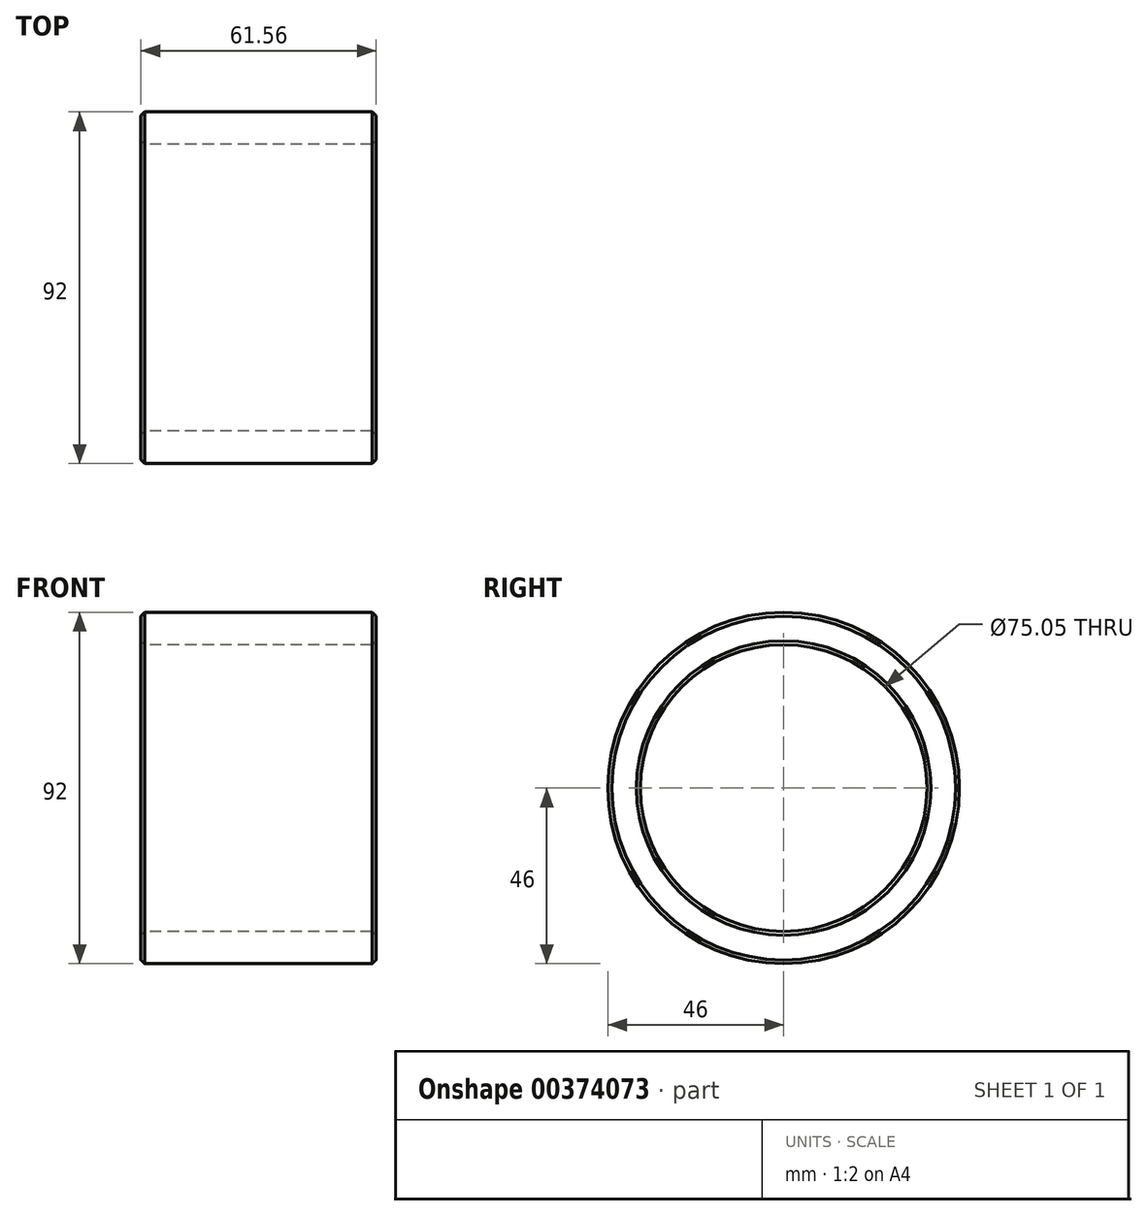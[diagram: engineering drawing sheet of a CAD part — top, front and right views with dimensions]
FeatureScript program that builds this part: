
annotation { "Feature Type Name" : "Feature", "Feature Type Description" : "" }
export const myFeature = defineFeature(function(context is Context, id is Id, definition is map)
    precondition{}
    {
        {
            var Q0;
            Q0=qCreatedBy(makeId("Right.planeOp"),FACE);
            var sketch = newSketch(context, id + "F0", { "sketchPlane" : qUnion([Q0])});
            skCircle(sketch, "E0", {"center": v(0, 0) * mm, "radius": 37.53 * mm});
            skCircle(sketch, "E1", {"center": v(0, 0) * mm, "radius": 46 * mm});
            skSolve(sketch);
        }
        {
            var Q0;
            Q0=qSketchRegion(id+"F0",true);
            extrude(context, id + "F1", {"entities" : qUnion([Q0]), "offsetDistance" : 25 * mm, "depth" : 61.56 * mm});
        }
        {
            var Q0;
            Q0=makeQuery(id+"F1.opExtrude","SWEPT_FACE",FACE,{"disambiguationData":[OSD([sQuery(id+"F0.wireOp",EDGE,"E1")])]});
            var Q1;
            Q1=makeQuery(id+"F1.opExtrude","CAP_EDGE",EDGE,{"disambiguationData":[OSD([sQuery(id+"F0.wireOp",EDGE,"E0")])],"isStart":false});
            var Q2;
            Q2=makeQuery(id+"F1.opExtrude","CAP_EDGE",EDGE,{"disambiguationData":[OSD([sQuery(id+"F0.wireOp",EDGE,"E0")])],"isStart":true});
            chamfer(context, id + "F2", {"entities" : qUnion([Q0, Q1, Q2]), "width" : 1 * mm, "tangentPropagation" : true});
        }
    });
